# Revit family: STH20962BR_27_40
name_source: partatom
category: Luminárias
units: mm (PartAtom-declared; Revit-internal decimal feet)

## family parameters
Compartilhado = Não
Corte com vazios quando carregada = Não
Cota do conector redondo = Utilizar diâmetro
Fonte luminosa = Não
Hospedeiro = Forro
Manter orientação da anotação = Não
Número OmniClass = 23.80.70.11
Ponto de cálculo do ambiente = Não
Sempre na vertical = Sim
Tipo de parte = Normal
Título OmniClass = Luminaries for Internal Lighting

## types (2) — shared parameters
Altura = 0.03 m
Comprimento = 2.01 m
Dimerização = Não dimerizável
Estrutura = Al - Branco
Fabricante = Stella
Fluxo Luminoso = 1140 lm
Grau de proteção (IP) = IP20
IRC (Índice de reprodução de cores) = >93 (R9 >60)
Largura = 0.03 m
Modelo = Archi
Potência = 12 W
Tensão Elétrica = 24V
URL = https://stella.com.br
Ângulo de Abertura = 110°
zero-valued in all types: Elevação padrão

## per-type parameters (varying)
| type | Fluxo Luminoso STH20962BR/27 | Fluxo Luminoso STH20962BR/40 | Luminoso | Referência | Temperatura da cor (K) |
| STH20962BR/27 - BRANCO - 2m - 2700K - 1140lm - 110° | Sim | Não | Luminoso - 2700K | STH20962BR/27 - BRANCO - 2m | 2700 K |
| STH20962BR/40 - BRANCO - 2m - 4000K - 1140lm - 110° | Não | Sim | Luminoso - 4000K | STH20962BR/40 - BRANCO - 2m | 4000 K |
